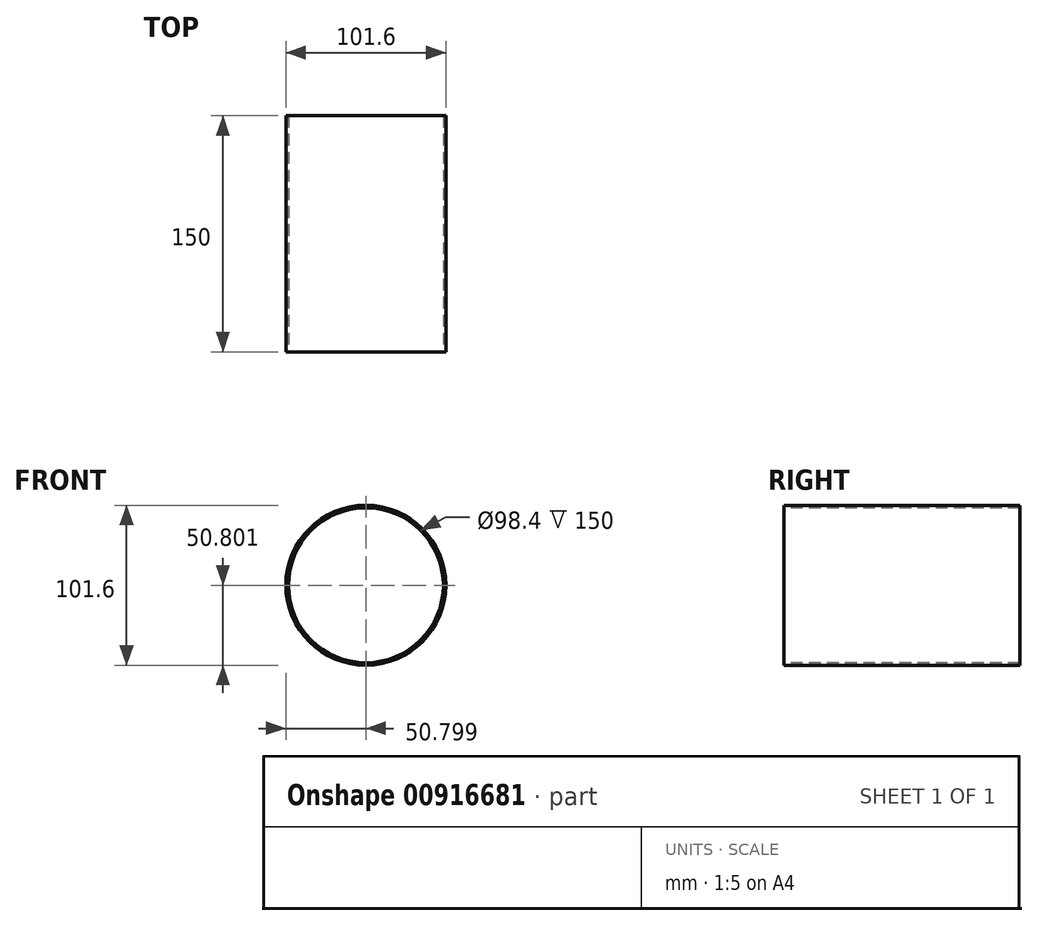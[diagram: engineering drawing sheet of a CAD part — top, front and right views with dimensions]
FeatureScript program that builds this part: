
annotation { "Feature Type Name" : "Feature", "Feature Type Description" : "" }
export const myFeature = defineFeature(function(context is Context, id is Id, definition is map)
    precondition{}
    {
        {
            var Q0;
            Q0=qCreatedBy(makeId("Front.planeOp"),FACE);
            var sketch = newSketch(context, id + "F0", { "sketchPlane" : qUnion([Q0])});
            skCircle(sketch, "E0", {"center": v(-59.36, 50.33) * mm, "radius": 50.8 * mm});
            skCircle(sketch, "E1", {"center": v(-59.36, 50.33) * mm, "radius": 49.2 * mm});
            skSolve(sketch);
        }
        {
            var Q0;
            Q0 = qSketchRegion(id + "F0", true);
            extrude(context, id + "F1", {"entities" : qUnion([Q0]), "oppositeDirection" : true, "depth" : 150 * mm, "offsetDistance" : 25 * mm});
        }
    });
